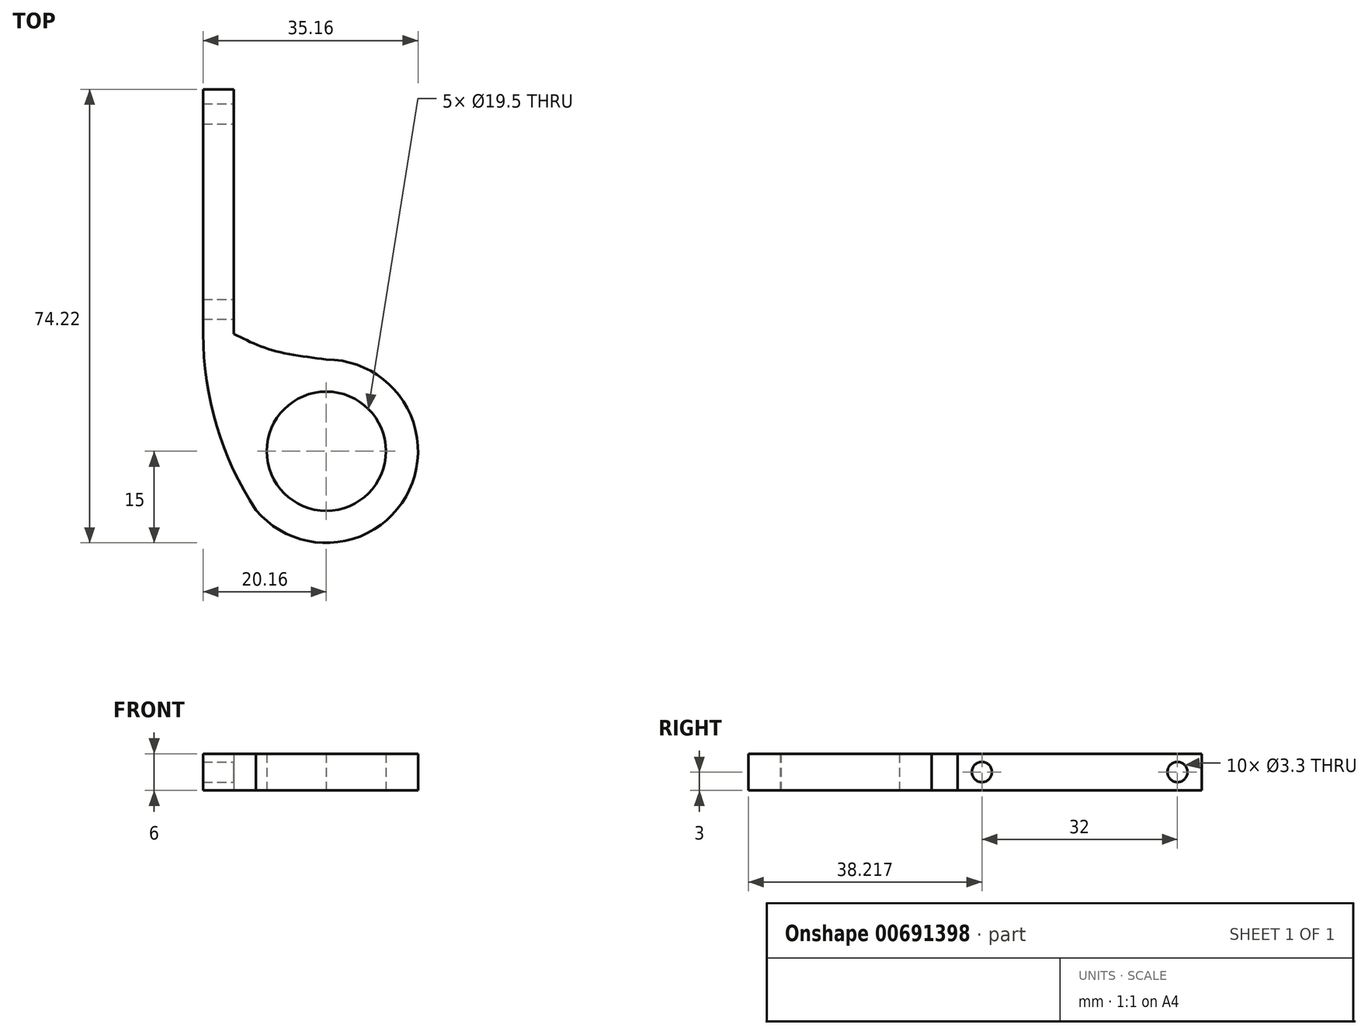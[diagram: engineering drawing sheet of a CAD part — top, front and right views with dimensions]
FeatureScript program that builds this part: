
annotation { "Feature Type Name" : "Feature", "Feature Type Description" : "" }
export const myFeature = defineFeature(function(context is Context, id is Id, definition is map)
    precondition{}
    {
        {
            var Q0;
            Q0=qCreatedBy(makeId("Top.planeOp"),FACE);
            var sketch = newSketch(context, id + "F0", { "sketchPlane" : qUnion([Q0])});
            skLineSegment(sketch, "E0.top", {"start": v(-15.16, 59.22) * mm, "end": v(-20.16, 59.22) * mm});
            skLineSegment(sketch, "E0.left", {"start": v(-15.16, 19.22) * mm, "end": v(-15.16, 59.22) * mm});
            skLineSegment(sketch, "E0.right", {"start": v(-20.16, 19.22) * mm, "end": v(-20.16, 59.22) * mm});
            skArc(sketch, "E1", {"start": v(-20.16, 19.22) * mm, "mid": v(-17.95, 4.16) * mm, "end": v(-11.5, -9.63) * mm});
            skFitSpline(sketch, "E2", {"points": [v(-15.16, 19.22) * mm, v(-9.21, 16.64) * mm, v(0, 15) * mm], "startDerivative": vector(12.23, -6.28) * mm, "endDerivative": vector(17.91, -2.28) * mm});
            skArc(sketch, "E3", {"start": v(-11.5, -9.63) * mm, "mid": v(13.6, -6.35) * mm, "end": v(0, 15) * mm});
            skCircle(sketch, "E4", {"center": v(0, 0) * mm, "radius": 9.75 * mm});
            skSolve(sketch);
        }
        {
            var Q0;
            Q0 = qSketchRegion(id + "F0", true);
            extrude(context, id + "F1", {"entities" : qUnion([Q0]), "depth" : 6 * mm, "offsetDistance" : 25 * mm});
        }
        {
            var Q0;
            Q0=qCreatedBy(makeId("Right.planeOp"),FACE);
            var sketch = newSketch(context, id + "F2", { "sketchPlane" : qUnion([Q0])});
            skPoint(sketch, "E5", {"position": v(55.22, 3) * mm});
            skPoint(sketch, "E6", {"position": v(23.22, 3) * mm});
            skSolve(sketch);
        }
        {
            var Q0;
            Q0=sQuery(id+"F2.wireOp",VERTEX,"E6");
            var Q1;
            Q1=sQuery(id+"F2.wireOp",VERTEX,"E5");
            var Q2;
            Q2=makeQuery(id+"F1.opExtrude","SWEPT_BODY",BODY,{"disambiguationData":[OSD([sQuery(id+"F0.wireOp",EDGE,"CXHavMvs-Qe8t-dgqm-4fli-VdthwaMgAqbL"),sQuery(id+"F0.wireOp",EDGE,"E0.top"),sQuery(id+"F0.wireOp",EDGE,"E0.left"),sQuery(id+"F0.wireOp",EDGE,"E0.right"),sQuery(id+"F0.wireOp",EDGE,"E1"),sQuery(id+"F0.wireOp",EDGE,"E2"),sQuery(id+"F0.wireOp",EDGE,"E3")])]});
            hole(context, id + "F3", {"style" : HoleStyle.SIMPLE, "endStyle" : HoleEndStyle.THROUGH, "standardTappedOrClearance" : lookupTablePath({ "standard" : "ISO", "fit" : "Normal", "size" : "M3", "type" : "Clearance" }), "standardBlindInLast" : lookupTablePath({ "fit" : "Standard", "standard" : "ISO", "size" : "M3", "type" : "Clearance" }), "holeDiameter" : 3.3 * mm, "majorDiameter" : 3 * mm, "isTappedThrough" : true, "tappedDepth" : 12 * mm, "tapClearance" : 3, "locations" : qUnion([Q0, Q1]), "scope" : qUnion([Q2])});
        }
    });
